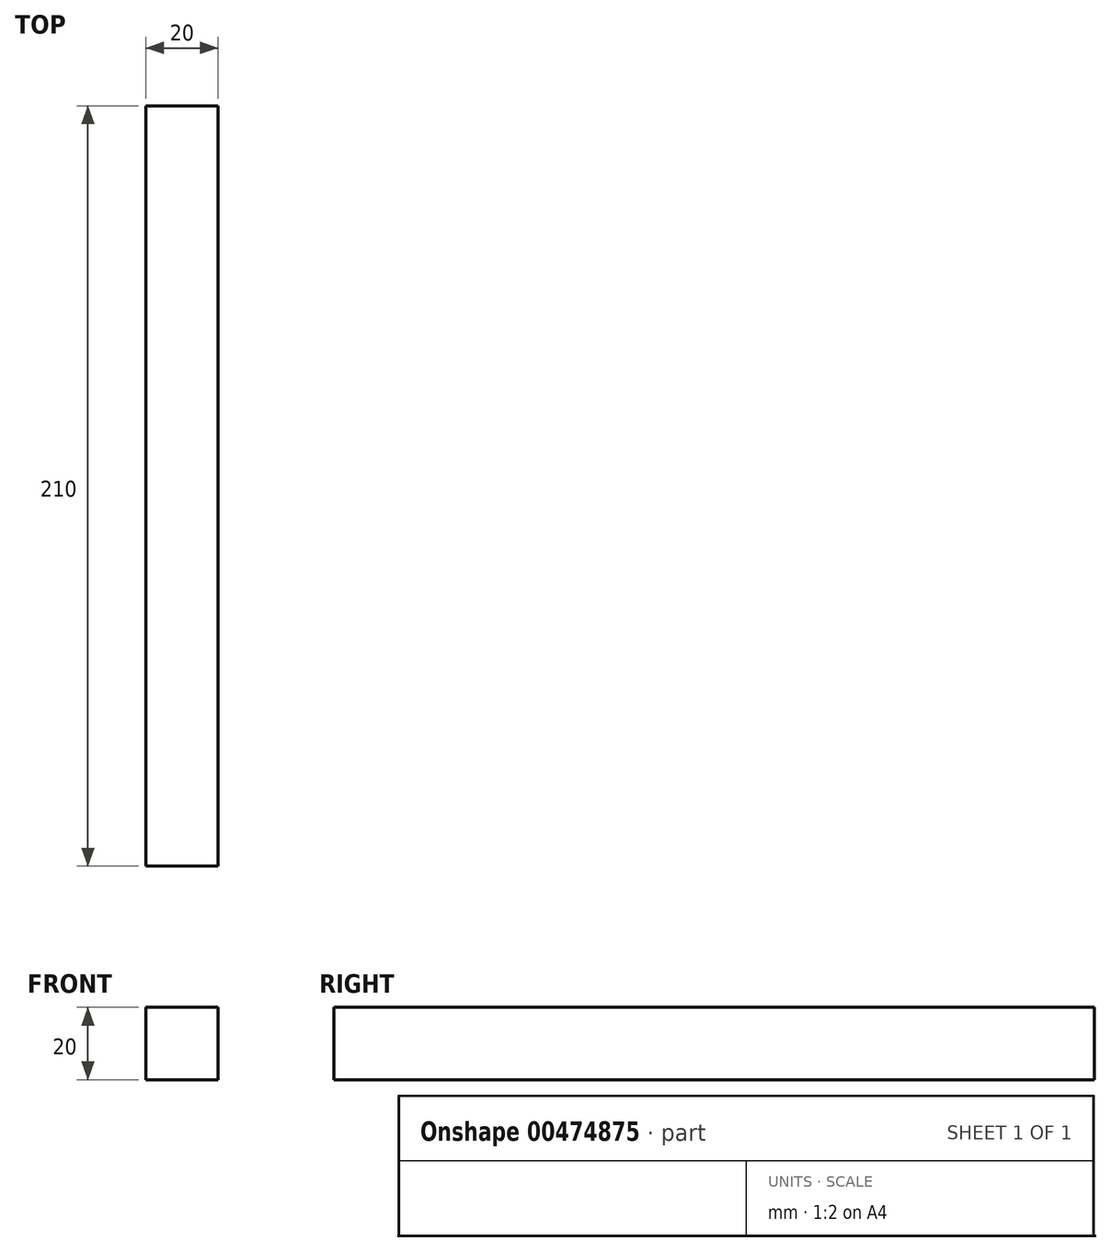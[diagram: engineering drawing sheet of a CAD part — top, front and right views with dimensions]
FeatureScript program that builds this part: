
annotation { "Feature Type Name" : "Feature", "Feature Type Description" : "" }
export const myFeature = defineFeature(function(context is Context, id is Id, definition is map)
    precondition{}
    {
        {
            var Q0;
            Q0=qCreatedBy(makeId("Front.planeOp"),FACE);
            var sketch = newSketch(context, id + "F0", { "sketchPlane" : qUnion([Q0])});
            skLineSegment(sketch, "E0.bottom", {"start": v(10, -10) * mm, "end": v(-10, -10) * mm});
            skLineSegment(sketch, "E0.top", {"start": v(10, 10) * mm, "end": v(-10, 10) * mm});
            skLineSegment(sketch, "E0.left", {"start": v(10, -10) * mm, "end": v(10, 10) * mm});
            skLineSegment(sketch, "E0.right", {"start": v(-10, -10) * mm, "end": v(-10, 10) * mm});
            skPoint(sketch, "E0.middle", {"position": v(0, 0) * mm});
            skSolve(sketch);
        }
        {
            var Q0;
            Q0 = qSketchRegion(id + "F0", true);
            extrude(context, id + "F1", {"entities" : qUnion([Q0]), "endBound" : BoundingType.SYMMETRIC, "depth" : 210 * mm});
        }
    });
